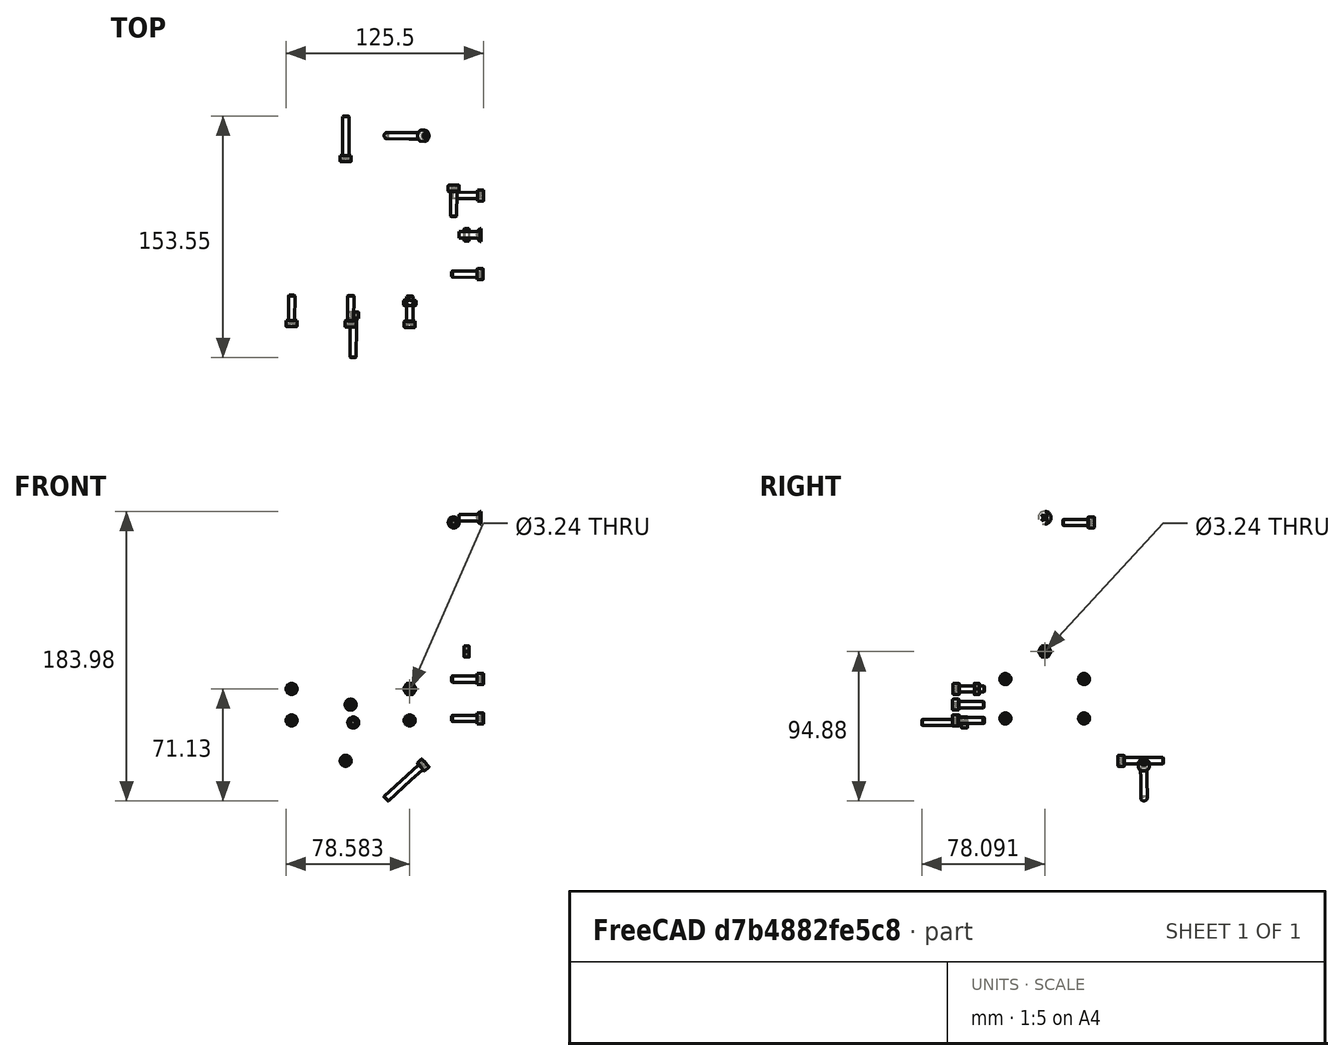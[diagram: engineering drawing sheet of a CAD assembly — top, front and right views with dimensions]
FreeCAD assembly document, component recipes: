
FREECAD ASSEMBLY — COMPONENT RECIPES ("RobotAssembly")

This assembly document has 52 components, labeled P0..P51 below (a component is one placed body or linked part). 4 of them carry a construction recipe — the FreeCAD feature program that regenerates the part from scratch, quoted from this document or its linked companion documents; the rest are supplied as boundary geometry only. No exploded tour is included for this assembly.
COMPONENT P0 — geometry summary ("Battery Mount"; no construction recipe available for this part):
  bounding box: 67.2 x 45.3 x 35.0 mm
  tessellated surface: 1,040 triangles
  volume: 39577 mm^3 (37% of its bounding box)
  symmetry: mirror-symmetric across its y mid-plane
COMPONENT P1 — geometry summary ("Bearing Wheel Mount"; no construction recipe available for this part):
  bounding box: 60.4 x 36.4 x 17.2 mm
  tessellated surface: 2,476 triangles
  volume: 15843 mm^3 (42% of its bounding box)
COMPONENT P2 — geometry summary ("Body"; no construction recipe available for this part):
  bounding box: 150.6 x 100.9 x 42.5 mm
  tessellated surface: 15,760 triangles
  volume: 188663 mm^3 (29% of its bounding box)
COMPONENT P3 — geometry summary ("Body Top"; no construction recipe available for this part):
  bounding box: 150.6 x 100.9 x 5.0 mm
  tessellated surface: 8,920 triangles
  volume: 66554 mm^3 (88% of its bounding box)
COMPONENT P4 — geometry summary ("Cat Toy Clamp"; no construction recipe available for this part):
  bounding box: 59.5 x 32.6 x 13.4 mm
  tessellated surface: 6,652 triangles
  volume: 22928 mm^3 (88% of its bounding box)
  symmetry: 2-fold rotationally symmetric about the x axis; mirror-symmetric across its z mid-plane
COMPONENT P5 — geometry summary ("Cat Toy Mount"; no construction recipe available for this part):
  bounding box: 100.1 x 95.0 x 49.3 mm
  tessellated surface: 9,540 triangles
  volume: 65342 mm^3 (14% of its bounding box)
  symmetry: mirror-symmetric across its y mid-plane
COMPONENT P6 — geometry summary ("Clamp"; no construction recipe available for this part):
  bounding box: 25.3 x 24.0 x 7.1 mm
  tessellated surface: 1,368 triangles
  volume: 1262 mm^3 (29% of its bounding box)
  symmetry: mirror-symmetric across its y mid-plane
COMPONENT P7 — geometry summary ("GUNCAIZHU_Ventilator_30x30x7,5_5V014"; no construction recipe available for this part):
  bounding box: 31.5 x 30.2 x 7.8 mm
  tessellated surface: 41,082 triangles
  volume: 3441 mm^3 (46% of its bounding box)
COMPONENT P8 — geometry summary ("am-3637 NeveRest Orbital 20 Gearmotor REV003"; no construction recipe available for this part):
  bounding box: 134.4 x 38.2 x 38.0 mm
  tessellated surface: 144,826 triangles
  volume: 110915 mm^3 (57% of its bounding box)
COMPONENT P9 — geometry summary ("M4x16-Screw026"; no construction recipe available for this part):
  bounding box: 20.0 x 7.0 x 7.0 mm
  tessellated surface: 5,082 triangles
  volume: 333 mm^3 (34% of its bounding box)
  symmetry: revolution-symmetric about the y axis through its bounding-box center; mirror-symmetric across its z mid-plane
COMPONENT P10 — geometry summary ("M4x14-Screw001"; no construction recipe available for this part):
  bounding box: 14.0 x 8.2 x 8.2 mm
  tessellated surface: 3,414 triangles
  volume: 224 mm^3 (24% of its bounding box)
  symmetry: mirror-symmetric across its y mid-plane, z mid-plane
COMPONENT P11 — geometry summary ("M4-Nut003"; no construction recipe available for this part):
  bounding box: 8.1 x 7.0 x 3.2 mm
  tessellated surface: 2,088 triangles
  volume: 107 mm^3 (58% of its bounding box)
COMPONENT P12 — geometry summary ("M4-Nut004"; no construction recipe available for this part):
  bounding box: 8.1 x 7.0 x 3.2 mm
  tessellated surface: 2,088 triangles
  volume: 107 mm^3 (58% of its bounding box)
  symmetry: 3-fold rotationally symmetric about the y axis
COMPONENT P13 — geometry summary ("M4-Nut006"; no construction recipe available for this part):
  bounding box: 8.1 x 7.0 x 3.2 mm
  tessellated surface: 2,088 triangles
  volume: 107 mm^3 (58% of its bounding box)
COMPONENT P14 — geometry summary ("M4-Nut007"; no construction recipe available for this part):
  bounding box: 8.1 x 7.0 x 3.2 mm
  tessellated surface: 2,088 triangles
  volume: 107 mm^3 (58% of its bounding box)
COMPONENT P15 — geometry summary ("M4-Nut008"; no construction recipe available for this part):
  bounding box: 8.1 x 7.0 x 3.2 mm
  tessellated surface: 2,088 triangles
  volume: 107 mm^3 (58% of its bounding box)
  symmetry: 3-fold rotationally symmetric about the y axis
COMPONENT P16 — geometry summary ("M4-Nut009"; no construction recipe available for this part):
  bounding box: 8.1 x 7.0 x 3.2 mm
  tessellated surface: 2,088 triangles
  volume: 107 mm^3 (58% of its bounding box)
COMPONENT P17 — geometry summary ("M4-Nut010"; no construction recipe available for this part):
  bounding box: 8.1 x 7.0 x 3.2 mm
  tessellated surface: 2,088 triangles
  volume: 107 mm^3 (58% of its bounding box)
COMPONENT P18 — geometry summary ("M4-Nut011"; no construction recipe available for this part):
  bounding box: 8.1 x 7.0 x 3.2 mm
  tessellated surface: 2,088 triangles
  volume: 107 mm^3 (58% of its bounding box)
  symmetry: 3-fold rotationally symmetric about the y axis
COMPONENT P19 — geometry summary ("M4-Nut012"; no construction recipe available for this part):
  bounding box: 8.1 x 7.0 x 3.2 mm
  tessellated surface: 2,088 triangles
  volume: 107 mm^3 (58% of its bounding box)
COMPONENT P20 — geometry summary ("M4x16-Screw034"; no construction recipe available for this part):
  bounding box: 20.0 x 7.0 x 7.0 mm
  tessellated surface: 5,082 triangles
  volume: 333 mm^3 (34% of its bounding box)
  symmetry: revolution-symmetric about the y axis through its bounding-box center; mirror-symmetric across its z mid-plane
COMPONENT P21 — geometry summary ("M4x16-Screw035"; no construction recipe available for this part):
  bounding box: 20.0 x 7.0 x 7.0 mm
  tessellated surface: 5,082 triangles
  volume: 333 mm^3 (34% of its bounding box)
  symmetry: revolution-symmetric about the y axis through its bounding-box center; mirror-symmetric across its z mid-plane
COMPONENT P22 — geometry summary ("M4x16-Screw036"; no construction recipe available for this part):
  bounding box: 20.0 x 7.0 x 7.0 mm
  tessellated surface: 5,082 triangles
  volume: 333 mm^3 (34% of its bounding box)
  symmetry: revolution-symmetric about the y axis through its bounding-box center; mirror-symmetric across its z mid-plane
COMPONENT P23 — geometry summary ("M4x16-Screw037"; no construction recipe available for this part):
  bounding box: 20.0 x 7.0 x 7.0 mm
  tessellated surface: 5,082 triangles
  volume: 333 mm^3 (34% of its bounding box)
  symmetry: revolution-symmetric about the y axis through its bounding-box center; mirror-symmetric across its z mid-plane
COMPONENT P24 — geometry summary ("M4x16-Screw038"; no construction recipe available for this part):
  bounding box: 20.0 x 7.0 x 7.0 mm
  tessellated surface: 5,082 triangles
  volume: 333 mm^3 (34% of its bounding box)
  symmetry: revolution-symmetric about the y axis through its bounding-box center; mirror-symmetric across its z mid-plane
COMPONENT P25 — geometry summary ("Motor Mount Right001"; no construction recipe available for this part):
  bounding box: 90.5 x 80.2 x 5.5 mm
  tessellated surface: 8,834 triangles
  volume: 22843 mm^3 (57% of its bounding box)
COMPONENT P26 — geometry summary ("Clamp001"; no construction recipe available for this part):
  bounding box: 28.4 x 10.2 x 7.1 mm
  tessellated surface: 1,368 triangles
  volume: 1262 mm^3 (61% of its bounding box)
  symmetry: mirror-symmetric across its y mid-plane
COMPONENT P27 — geometry summary ("Wheel001"; no construction recipe available for this part):
  bounding box: 55.0 x 55.0 x 21.6 mm
  tessellated surface: 19,376 triangles
  volume: 31320 mm^3 (48% of its bounding box)
COMPONENT P28 — geometry summary ("M4x30-Screw001"; no construction recipe available for this part):
  bounding box: 28.4 x 26.5 x 7.0 mm
  tessellated surface: 5,284 triangles
  volume: 509 mm^3 (10% of its bounding box)
COMPONENT P29 — geometry summary ("Bearing Wheel Mount001"; no construction recipe available for this part):
  bounding box: 60.4 x 36.4 x 17.2 mm
  tessellated surface: 2,476 triangles
  volume: 15843 mm^3 (42% of its bounding box)
COMPONENT P30 — geometry summary ("M4x16-Screw119"; no construction recipe available for this part):
  bounding box: 29.0 x 7.0 x 7.0 mm
  tessellated surface: 5,284 triangles
  volume: 446 mm^3 (31% of its bounding box)
  symmetry: revolution-symmetric about the y axis through its bounding-box center
COMPONENT P31 — geometry summary ("M4x16-Screw120"; no construction recipe available for this part):
  bounding box: 29.0 x 7.0 x 7.0 mm
  tessellated surface: 5,284 triangles
  volume: 446 mm^3 (31% of its bounding box)
  symmetry: revolution-symmetric about the y axis through its bounding-box center
COMPONENT P32 — geometry summary ("M4x16-Screw121"; no construction recipe available for this part):
  bounding box: 29.0 x 7.0 x 7.0 mm
  tessellated surface: 5,284 triangles
  volume: 446 mm^3 (31% of its bounding box)
  symmetry: revolution-symmetric about the y axis through its bounding-box center
COMPONENT P33 — geometry summary ("M4x16-Screw123"; no construction recipe available for this part):
  bounding box: 29.0 x 7.0 x 7.0 mm
  tessellated surface: 5,284 triangles
  volume: 446 mm^3 (31% of its bounding box)
COMPONENT P34 — geometry summary ("1609-0613-0008"; no construction recipe available for this part):
  bounding box: 13.0 x 13.0 x 6.1 mm
  tessellated surface: 16,484 triangles
  volume: 513 mm^3 (50% of its bounding box)
  symmetry: 2-fold rotationally symmetric about the x axis; revolution-symmetric about the y axis through its bounding-box center; 2-fold rotationally symmetric about the z axis; mirror-symmetric across its x mid-plane, y mid-plane, z mid-plane
COMPONENT P35 — geometry summary ("StringGuard001"; no construction recipe available for this part):
  bounding box: 15.0 x 12.5 x 8.1 mm
  tessellated surface: 2,628 triangles
  volume: 615 mm^3 (40% of its bounding box)
  symmetry: 2-fold rotationally symmetric about the z axis; mirror-symmetric across its x mid-plane, y mid-plane
COMPONENT P36 — geometry summary ("am-3637 NeveRest Orbital 20 Gearmotor REV004"; no construction recipe available for this part):
  bounding box: 134.4 x 38.2 x 38.0 mm
  tessellated surface: 144,826 triangles
  volume: 110915 mm^3 (57% of its bounding box)
COMPONENT P37 — geometry summary ("Motor Mount Right"; no construction recipe available for this part):
  bounding box: 90.5 x 80.2 x 5.5 mm
  tessellated surface: 8,834 triangles
  volume: 22843 mm^3 (57% of its bounding box)
COMPONENT P38 — geometry summary ("Passive Claw Left"; no construction recipe available for this part):
  bounding box: 57.6 x 35.3 x 21.5 mm
  tessellated surface: 2,676 triangles
  volume: 8897 mm^3 (20% of its bounding box)
COMPONENT P39 — geometry summary ("Passive Claw Right"; no construction recipe available for this part):
  bounding box: 57.6 x 35.3 x 21.5 mm
  tessellated surface: 2,676 triangles
  volume: 8897 mm^3 (20% of its bounding box)
COMPONENT P40 — geometry summary ("Ras Pi 3B+179"; no construction recipe available for this part):
  bounding box: 89.4 x 58.8 x 19.1 mm
  tessellated surface: 24,256 triangles
  volume: 25288 mm^3 (25% of its bounding box)
COMPONENT P41 — recipe-attached ("SAR2-20_b", a linked part whose construction recipe lives in a companion FreeCAD document of the same project; that document's serialized recipe follows).
Construction recipe (the companion document, serialized — sketch geometry with constraints, then the solid features built on it; lengths are millimeters unless a unit is written):

FCSTD DOCUMENT  (FreeCAD 1.1R42987 (Git))
Label: MISUMI-Sar220
License: All rights reserved
LicenseURL: https://en.wikipedia.org/wiki/All_rights_reserved
objects: Part::Feature×2, Part::DatumPoint×2
note: 2 computed .brp shape members not serialized (recipe doc carries the construction recipe); baked Part::Feature solids carry a one-line shape summary decoded from their .brp

FEATURE [Part::Feature] Part__Feature  label="SAR2-20_r"
  Placement = pos=(1.89152,0.668144,-0.306396) rot=(0,0,1;0rad)
  shape: bbox 5.8 x 12.1 x 200 mm, 38 faces (baked)
FEATURE [Part::Feature] Part__Feature001  label="SAR2-20_b"
  Placement = pos=(7.09149,-3.28186,-0.306396) rot=(0,0,1;0rad)
  shape: bbox 7.4 x 20 x 200 mm, 93 faces (baked)
FEATURE [Part::DatumPoint] DatumPoint
  AttacherType = Attacher::AttachEnginePoint
  AttachmentSupport = -> [Part__Feature001]
  MapMode = 37
  Placement = pos=(2.19373,6.71814,199.694) rot=(0,0,1;0rad)
FEATURE [Part::DatumPoint] DatumPoint001
  AttacherType = Attacher::AttachEnginePoint
  AttachmentSupport = -> [Part__Feature]
  MapMode = 37
  Placement = pos=(5.18893,6.71814,199.694) rot=(0,0,1;0rad)
COMPONENT P42 — same part as P41; its construction recipe is shown at P41.
COMPONENT P43 — geometry summary ("Slides Motor Mount"; no construction recipe available for this part):
  bounding box: 57.1 x 55.0 x 36.3 mm
  tessellated surface: 7,668 triangles
  volume: 23194 mm^3 (20% of its bounding box)
  symmetry: mirror-symmetric across its x mid-plane
COMPONENT P44 — geometry summary ("Slides Mount"; no construction recipe available for this part):
  bounding box: 139.5 x 60.0 x 25.1 mm
  tessellated surface: 4,146 triangles
  volume: 36849 mm^3 (18% of its bounding box)
COMPONENT P45 — geometry summary ("Slides Plate"; no construction recipe available for this part):
  bounding box: 189.0 x 78.0 x 5.5 mm
  tessellated surface: 4,636 triangles
  volume: 36980 mm^3 (46% of its bounding box)
  symmetry: mirror-symmetric across its x mid-plane
COMPONENT P46 — geometry summary ("Spool"; no construction recipe available for this part):
  bounding box: 35.2 x 35.2 x 35.0 mm
  tessellated surface: 8,372 triangles
  volume: 14357 mm^3 (33% of its bounding box)
COMPONENT P47 — recipe-attached ("Spool CHub", a linked part whose construction recipe lives in a companion FreeCAD document of the same project; that document's serialized recipe follows).
Construction recipe (the companion document, serialized — sketch geometry with constraints, then the solid features built on it; lengths are millimeters unless a unit is written):

FCSTD DOCUMENT  (FreeCAD 1.1R42863 (Git))
Label: Spool
License: All rights reserved
LicenseURL: https://en.wikipedia.org/wiki/All_rights_reserved
objects: Sketcher::SketchObject×7, PartDesign::Pad×5, App::Point×2, PartDesign::Pocket×2, PartDesign::Chamfer×2, PartDesign::Body×2, Part::DatumPlane×1, PartDesign::PolarPattern×1, PartDesign::SubShapeBinder×1, PartDesign::Fillet×1
note: 49 computed .brp shape members not serialized (recipe doc carries the construction recipe); baked Part::Feature solids carry a one-line shape summary decoded from their .brp
EXTERNAL_REF file=../Variables.FCStd obj=Spreadsheet

FEATURE [App::Point] Origin001
  Role = Origin
FEATURE [Sketcher::SketchObject] Sketch
  ArcFitTolerance = 1e-06
  AttachmentSupport = -> [XY_Plane]
  ExternalTypes = [0]
  FullyConstrained = true
  MakeInternals = false
  MapMode = 5
  expr: Constraints[13] = Variables#Spreadsheet.SpoolInnerDiam
  expr: Constraints[7] = Variables#Spreadsheet.M4TapDiam
  sketch-geometry (7):
    g0: Circle CenterX=-2.798e-13 CenterY=0 CenterZ=0 NormalX=0 NormalY=0 NormalZ=1 AngleXU=0 Radius=17.5
    g1: LineSegment [constr] StartX=9 StartY=5 StartZ=0 EndX=9 EndY=-5 EndZ=0
    g2: GeomPoint [constr] X=9 Y=0 Z=0
    g3: Circle CenterX=9 CenterY=5 CenterZ=0 NormalX=0 NormalY=0 NormalZ=1 AngleXU=0 Radius=1.8
    g4: Circle CenterX=9 CenterY=-5 CenterZ=0 NormalX=0 NormalY=0 NormalZ=1 AngleXU=0 Radius=1.8
    g5: Circle CenterX=-2.798e-13 CenterY=0 CenterZ=0 NormalX=0 NormalY=0 NormalZ=1 AngleXU=0 Radius=3.125
    g6: Circle [constr] CenterX=-2.798e-13 CenterY=0 CenterZ=0 NormalX=0 NormalY=0 NormalZ=1 AngleXU=0 Radius=7.5
  constraints (15):
    c: Diameter(g0) = 35
    c: Coincident(g0,g-1)
    c: Distance(g1) = 10
    c: Vertical(g1)
    c: Symmetric(g1,g1,g2)
    c: PointOnObject(g2,g-1)
    c: Coincident(g3,g1)
    c: Diameter(g3) = 3.6
    c: Coincident(g4,g1)
    c: Equal(g4,g3)
    c: Diameter(g5) = 6.25
    c: Coincident(g5,g0)
    c: Coincident(g6,g0)
    c: Diameter(g6) = 15
    c: Distance(g2,g6) = 1.5
FEATURE [PartDesign::Pad] Pad
  Direction = (0,0,1)
  Length = 5
  Length2 = 10
  Profile = -> Sketch
  ReferenceAxis = -> Sketch [N_Axis]
  Refine = true
  Suppressed = false
  Type = 0
  expr: Length = Variables#Spreadsheet.SpoolWallThickness
FEATURE [Sketcher::SketchObject] Sketch001
  ArcFitTolerance = 1e-06
  AttachmentSupport = -> [Pad]
  ExternalGeometry = -> [Pad]
  ExternalTypes = [0]
  FullyConstrained = true
  MakeInternals = false
  MapMode = 5
  Placement = pos=(0,0,0) rot=(1,0,0;3.14159rad)
  expr: Constraints[0] = Variables#Spreadsheet.SpoolInnerDiam
  sketch-geometry (1):
    g0: Circle CenterX=0 CenterY=0 CenterZ=0 NormalX=0 NormalY=0 NormalZ=1 AngleXU=0 Radius=7.5
  constraints (2):
    c: Diameter(g0) = 15
    c: Coincident(g0,g-1)
FEATURE [PartDesign::Pad] Pad001
  BaseFeature = -> Pad
  Direction = (0,0,-1)
  Length = 35
  Length2 = 10
  Profile = -> Sketch001
  ReferenceAxis = -> Sketch001 [N_Axis]
  Refine = true
  Reversed = true
  Suppressed = false
  Type = 0
  expr: Length = Variables#Spreadsheet.SpoolThickness
FEATURE [Sketcher::SketchObject] Sketch002
  ArcFitTolerance = 1e-06
  AttachmentSupport = -> [Pad001]
  ExternalGeometry = -> [Pad001]
  ExternalTypes = [0,0]
  FullyConstrained = true
  MakeInternals = false
  MapMode = 5
  Placement = pos=(0,0,35) rot=(0,0,1;0rad)
FEATURE [PartDesign::Pad] Pad002
  BaseFeature = -> Pad001
  Direction = (0,0,1)
  Length = 5
  Length2 = 10
  Profile = -> Sketch002
  ReferenceAxis = -> Sketch002 [N_Axis]
  Refine = true
  Reversed = true
  Suppressed = false
  Type = 0
  expr: Length = Variables#Spreadsheet.SpoolWallThickness
FEATURE [Part::DatumPlane] DatumPlane
  AttachmentSupport = -> [Pad002]
  MapMode = 45
  Placement = pos=(-9e-16,0,17.5) rot=(0,0,1;0rad)
FEATURE [Sketcher::SketchObject] Sketch003
  ArcFitTolerance = 1e-06
  AttachmentSupport = -> [DatumPlane]
  ExternalGeometry = -> [Pad002]
  ExternalTypes = [0,0]
  FullyConstrained = true
  MakeInternals = false
  MapMode = 5
  Placement = pos=(-9e-16,0,17.5) rot=(0,0,1;0rad)
FEATURE [PartDesign::Pad] Pad003
  BaseFeature = -> Pad002
  Direction = (0,0,1)
  Length = 5
  Length2 = 10
  Midplane = true
  Profile = -> Sketch003
  ReferenceAxis = -> Sketch003 [N_Axis]
  Refine = true
  Suppressed = false
  Type = 0
  expr: Length = Variables#Spreadsheet.SpoolWallThickness
FEATURE [Sketcher::SketchObject] Sketch004
  ArcFitTolerance = 1e-06
  AttachmentSupport = -> [Pad003]
  ExternalGeometry = -> [Pad003]
  ExternalTypes = [0,0]
  FullyConstrained = true
  MakeInternals = false
  MapMode = 5
  Placement = pos=(0,0,20) rot=(0,0,1;0rad)
  sketch-geometry (5):
    g0: LineSegment [constr] StartX=9.5 StartY=-3 StartZ=0 EndX=9.5 EndY=3 EndZ=0
    g1: Circle CenterX=9.5 CenterY=-3 CenterZ=0 NormalX=0 NormalY=0 NormalZ=1 AngleXU=0 Radius=1.75
    g2: Circle CenterX=9.5 CenterY=3 CenterZ=0 NormalX=0 NormalY=0 NormalZ=1 AngleXU=0 Radius=1.75
    g3: GeomPoint [constr] X=7.5 Y=0 Z=0
    g4: GeomPoint [constr] X=9.5 Y=0 Z=0
  constraints (11):
    c: Vertical(g0)
    c: DistanceY(g0,g0) = 6
    c: Diameter(g1) = 3.5
    c: Coincident(g1,g0)
    c: Coincident(g2,g0)
    c: Equal(g1,g2)
    c: PointOnObject(g3,g-3)
    c: Symmetric(g0,g0,g4)
    c: PointOnObject(g3,g-1)
    c: PointOnObject(g4,g-1)
    c: DistanceX(g3,g4) = 2
FEATURE [PartDesign::Pocket] Pocket
  BaseFeature = -> Pad003
  Direction = (0,0,-1)
  Length = 0
  Length2 = 5
  Profile = -> Sketch004
  ReferenceAxis = -> Sketch004 [N_Axis]
  Refine = true
  Suppressed = false
  Type = 3
  UpToFace = -> Pad003 [Face10]
FEATURE [PartDesign::PolarPattern] PolarPattern
  Angle = 360
  Axis = -> Sketch004 [N_Axis]
  BaseFeature = -> Pocket
  Mode = 0
  Occurrences = 4
  Offset = 120
  Originals = -> [Pocket]
  Refine = true
  Suppressed = false
  TransformMode = 0
FEATURE [PartDesign::Chamfer] Chamfer
  Angle = 45
  Base = -> PolarPattern [Edge19,Edge30]
  BaseFeature = -> PolarPattern
  ChamferType = 0
  FlipDirection = false
  Refine = true
  Size = 2
  Size2 = 1
  SupportTransform = false
  Suppressed = false
  UseAllEdges = false
  expr: Size = Variables#Spreadsheet.SpoolWallThickness / 2 - 0.5
FEATURE [PartDesign::Chamfer] Chamfer001
  Angle = 45
  Base = -> Chamfer [Edge35,Edge41]
  BaseFeature = -> Chamfer
  ChamferType = 0
  FlipDirection = false
  Refine = true
  Size = 4
  Size2 = 1
  SupportTransform = false
  Suppressed = false
  UseAllEdges = false
  expr: Size = Variables#Spreadsheet.SpoolWallThickness - 1
FEATURE [PartDesign::Body] Body  label="Spool"
  AllowCompound = true
  Group = -> [Sketch,Pad,Sketch001,Pad001,Sketch002,Pad002,DatumPlane,Sketch003,Pad003,Sketch004,Pocket,PolarPattern,Chamfer,Chamfer001]
  Origin = -> Origin
  Tip = -> Chamfer001
FEATURE [App::Point] Origin003
  Role = Origin
FEATURE [PartDesign::SubShapeBinder] Binder
  BindCopyOnChange = 0
  BindMode = 0
  ClaimChildren = false
  Context = -> Body001 [Binder.]
  Fuse = false
  MakeFace = true
  OffsetFill = false
  OffsetIntersection = false
  OffsetJoinType = 0
  OffsetOpenResult = false
  PartialLoad = false
  Refine = true
  Relative = true
  Support = -> [Body]
  _Version = 2
FEATURE [Sketcher::SketchObject] Sketch005
  ArcFitTolerance = 1e-06
  AttachmentSupport = -> [Binder]
  ExternalGeometry = -> [Binder]
  ExternalTypes = [0,0,0]
  FullyConstrained = false
  MakeInternals = false
  MapMode = 5
  Placement = pos=(0,0,0) rot=(1,0,0;3.14159rad)
  expr: Constraints[34] = Variables#Spreadsheet.M4ThroughBoreDiam
  sketch-geometry (16):
    g0: ArcOfCircle CenterX=9 CenterY=5 CenterZ=0 NormalX=0 NormalY=0 NormalZ=1 AngleXU=0 Radius=4 StartAngle=-9e-16 EndAngle=1.90109
    g1: ArcOfCircle CenterX=9 CenterY=-5 CenterZ=0 NormalX=0 NormalY=0 NormalZ=1 AngleXU=0 Radius=4 StartAngle=4.38209 EndAngle=6.28319
    g2: LineSegment StartX=13 StartY=-5 StartZ=0 EndX=13 EndY=5 EndZ=0
    g3: LineSegment StartX=-11.5 StartY=7 StartZ=0 EndX=2.5 EndY=7 EndZ=0
    g4: LineSegment StartX=2.5 StartY=7 StartZ=0 EndX=7.7027 EndY=8.78378 EndZ=0
    g5: LineSegment StartX=-11.5 StartY=-7 StartZ=0 EndX=2.5 EndY=-7 EndZ=0
    g6: LineSegment StartX=2.5 StartY=-7 StartZ=0 EndX=7.7027 EndY=-8.78378 EndZ=0
    g7: GeomPoint X=0.731343 Y=-5.50967 Z=0
    g8: LineSegment StartX=-11.5 StartY=-7 StartZ=0 EndX=-11.5 EndY=-1.5 EndZ=0
    g9: ArcOfCircle CenterX=0 CenterY=0 CenterZ=0 NormalX=0 NormalY=0 NormalZ=1 AngleXU=0 Radius=3.075 StartAngle=3.65117 EndAngle=8.9152
    g10: LineSegment StartX=-11.5 StartY=7 StartZ=0 EndX=-11.5 EndY=1.5 EndZ=0
    g11: LineSegment StartX=-11.5 StartY=1.5 StartZ=0 EndX=-2.68433 EndY=1.5 EndZ=0
    g12: LineSegment StartX=-11.5 StartY=-1.5 StartZ=0 EndX=-2.68433 EndY=-1.5 EndZ=0
    g13: GeomPoint X=-11.5 Y=0 Z=0
    g14: Circle CenterX=9 CenterY=5 CenterZ=0 NormalX=0 NormalY=0 NormalZ=1 AngleXU=0 Radius=2.175
    g15: Circle CenterX=9 CenterY=-5 CenterZ=0 NormalX=0 NormalY=0 NormalZ=1 AngleXU=0 Radius=2.175
  constraints (37):
    c: Coincident(g0,g-3)
    c: Coincident(g1,g-4)
    c: Tangent(g2,g1) = -1.5708
    c: Tangent(g2,g0) = -1.5708
    c: Vertical(g2)
    c: Horizontal(g3)
    c: Coincident(g4,g3)
    c: Horizontal(g5)
    c: Coincident(g6,g5)
    c: Tangent(g6,g1) = -1.5708
    c: Tangent(g4,g0) = 1.5708
    c: Vertical(g3,g5)
    c: Vertical(g5,g3)
    c: Equal(g4,g6)
    c: DistanceX(g5,g5) = 14
    c: Distance(g5,g-2) = 2.5
    c: Coincident(g8,g5)
    c: Vertical(g8)
    c: Coincident(g9,g-1)
    c: Horizontal(g9,g8)
    c: Coincident(g10,g3)
    c: Vertical(g10)
    c: Coincident(g11,g10)
    c: Horizontal(g11)
    c: Coincident(g12,g8)
    c: Coincident(g12,g9)
    c: PointOnObject(g13,g-1)
    c: Symmetric(g10,g8,g13)
    c: Distance(g11,g12) = 3
    c: Distance(g3,g5) = 14
    c: Radius(g0) = 4
    c: Coincident(g9,g11)
    c: Radius(g9) = 3.075
    c: Coincident(g14,g0)
    c: Diameter(g14) = 4.35
    c: Coincident(g15,g1)
    c: Equal(g14,g15)
FEATURE [PartDesign::Pad] Pad004
  Direction = (0,0,-1)
  Length = 9
  Length2 = 10
  Profile = -> Sketch005
  ReferenceAxis = -> Sketch005 [N_Axis]
  Refine = true
  Suppressed = false
  Type = 0
FEATURE [Sketcher::SketchObject] Sketch006
  ArcFitTolerance = 1e-06
  AttachmentSupport = -> [Pad004]
  ExternalGeometry = -> [Pad004]
  ExternalTypes = [0]
  FullyConstrained = true
  MakeInternals = false
  MapMode = 5
  Placement = pos=(0,7,0) rot=(0,0.707107,0.707107;3.14159rad)
  expr: Constraints[1] = Variables#Spreadsheet.M4ThroughBoreDiam
  sketch-geometry (2):
    g0: GeomPoint [constr] X=11.5 Y=-4.5 Z=0
    g1: Circle CenterX=7.5 CenterY=-4.5 CenterZ=0 NormalX=0 NormalY=0 NormalZ=1 AngleXU=0 Radius=2.175
  constraints (4):
    c: Symmetric(g-3,g-3,g0)
    c: Diameter(g1) = 4.35
    c: Horizontal(g1,g0)
    c: DistanceX(g1,g0) = 4
FEATURE [PartDesign::Pocket] Pocket001
  BaseFeature = -> Pad004
  Direction = (0,-1,2e-16)
  Length = 0
  Length2 = 5
  Profile = -> Sketch006
  ReferenceAxis = -> Sketch006 [N_Axis]
  Refine = true
  Suppressed = false
  Type = 3
  UpToFace = -> Pad004 [Face7]
FEATURE [PartDesign::Fillet] Fillet
  Base = -> Pocket001 [Edge41,Edge43,Edge6,Edge1]
  BaseFeature = -> Pocket001
  Radius = 0.75
  Refine = true
  SupportTransform = false
  Suppressed = false
  UseAllEdges = false
FEATURE [PartDesign::Body] Body001  label="Spool CHub"
  AllowCompound = true
  Group = -> [Binder,Sketch005,Pad004,Sketch006,Pocket001,Fillet]
  Origin = -> Origin002
  Tip = -> Fillet
COMPONENT P48 — geometry summary ("StringGuard"; no construction recipe available for this part):
  bounding box: 15.0 x 12.5 x 8.1 mm
  tessellated surface: 2,628 triangles
  volume: 615 mm^3 (40% of its bounding box)
  symmetry: 2-fold rotationally symmetric about the z axis; mirror-symmetric across its y mid-plane
COMPONENT P49 — geometry summary ("Wheel"; no construction recipe available for this part):
  bounding box: 55.0 x 55.0 x 21.8 mm
  tessellated surface: 19,376 triangles
  volume: 31320 mm^3 (48% of its bounding box)
COMPONENT P50 — recipe-attached ("1609-0613-0007", a linked part whose construction recipe lives in a companion FreeCAD document of the same project; that document's serialized recipe follows).
Construction recipe (the companion document, serialized — sketch geometry with constraints, then the solid features built on it; lengths are millimeters unless a unit is written):

FCSTD DOCUMENT  (FreeCAD 1.1R42987 (Git))
Label: V-Groove
License: All rights reserved
LicenseURL: https://en.wikipedia.org/wiki/All_rights_reserved
objects: Sketcher::SketchObject×5, PartDesign::Pad×4, Part::Feature×3, App::Point×2, App::Part×1, PartDesign::SubShapeBinder×1, Part::DatumPlane×1, PartDesign::Pocket×1, PartDesign::Mirrored×1, PartDesign::Body×1
note: 32 computed .brp shape members not serialized (recipe doc carries the construction recipe); baked Part::Feature solids carry a one-line shape summary decoded from their .brp
EXTERNAL_REF file=../Variables.FCStd obj=Spreadsheet

FEATURE [Part::Feature] Part__Feature  label="1609-0613-0004"
  shape: bbox 9.277 x 0.3004 x 9.277 mm, 8 faces (baked)
FEATURE [Part::Feature] Part__Feature001  label="1609-0613-0005"
  shape: bbox 9.277 x 0.3004 x 9.277 mm, 8 faces (baked)
FEATURE [Part::Feature] Part__Feature002  label="1609-0613-0006"
  shape: bbox 13 x 6 x 13 mm, 66 faces (baked)
FEATURE [App::Part] _609_0613_0004  label="1609-0613-0007"
  Group = -> [Part__Feature,Part__Feature001,Part__Feature002]
  Origin = -> Origin
FEATURE [App::Point] Origin001
  Role = Origin
FEATURE [App::Point] Origin003
  Role = Origin
FEATURE [PartDesign::SubShapeBinder] Binder
  BindCopyOnChange = 0
  BindMode = 0
  ClaimChildren = false
  Context = -> Body [Binder.]
  Fuse = false
  MakeFace = true
  OffsetFill = false
  OffsetIntersection = false
  OffsetJoinType = 0
  OffsetOpenResult = false
  PartialLoad = false
  Refine = true
  Relative = true
  Support = -> [_609_0613_0004]
  _Version = 2
FEATURE [Sketcher::SketchObject] Sketch
  ArcFitTolerance = 1e-06
  AttachmentOffset = pos=(0,0,0.25) rot=(0,0,1;0rad)
  AttachmentSupport = -> [Binder]
  ExternalTypes = [0]
  FullyConstrained = true
  MakeInternals = false
  MapMode = 5
  Placement = pos=(0,-0.25,1e-16) rot=(1,0,0;1.5708rad)
  expr: Constraints[1] = Variables#Spreadsheet.M4ThroughBoreDiam
  sketch-geometry (2):
    g0: Circle CenterX=0 CenterY=0 CenterZ=0 NormalX=0 NormalY=0 NormalZ=1 AngleXU=0 Radius=2.175
    g1: Circle CenterX=0 CenterY=0 CenterZ=0 NormalX=0 NormalY=0 NormalZ=1 AngleXU=0 Radius=2.75
  constraints (4):
    c: Coincident(g0,g-1)
    c: Diameter(g0) = 4.35
    c: Coincident(g1,g0)
    c: Diameter(g1) = 5.5
FEATURE [PartDesign::Pad] Pad
  Direction = (0,-1,2e-16)
  Length = 1
  Length2 = 10
  Profile = -> Sketch
  ReferenceAxis = -> Sketch [N_Axis]
  Refine = true
  Suppressed = false
  Type = 0
FEATURE [Sketcher::SketchObject] Sketch001
  ArcFitTolerance = 1e-06
  AttachmentSupport = -> [Pad]
  ExternalGeometry = -> [Pad]
  ExternalTypes = [0]
  FullyConstrained = true
  MakeInternals = false
  MapMode = 5
  Placement = pos=(0,-1.25,3e-16) rot=(1,0,0;1.5708rad)
  sketch-geometry (4):
    g0: ArcOfCircle CenterX=0 CenterY=-4.3033e-12 CenterZ=0 NormalX=0 NormalY=0 NormalZ=1 AngleXU=0 Radius=4 StartAngle=3.14159 EndAngle=6.28319
    g1: LineSegment StartX=4 StartY=-6.67326e-11 StartZ=0 EndX=4 EndY=8 EndZ=0
    g2: LineSegment StartX=4 StartY=8 StartZ=0 EndX=-4 EndY=8 EndZ=0
    g3: LineSegment StartX=-4 StartY=8 StartZ=0 EndX=-4 EndY=-7.6463e-12 EndZ=0
  constraints (10):
    c: Coincident(g0,g-1)
    c: Vertical(g1)
    c: Coincident(g2,g1)
    c: Horizontal(g2)
    c: Coincident(g3,g2)
    c: Vertical(g3)
    c: DistanceY(g1,g1) = 8
    c: Diameter(g0) = 8
    c: Tangent(g1,g0) = -1.5708
    c: Tangent(g3,g0) = -1.5708
FEATURE [PartDesign::Pad] Pad001
  BaseFeature = -> Pad
  Direction = (0,-1,2e-16)
  Length = 2
  Length2 = 10
  Profile = -> Sketch001
  ReferenceAxis = -> Sketch001 [N_Axis]
  Refine = true
  Suppressed = false
  Type = 0
FEATURE [Sketcher::SketchObject] Sketch002
  ArcFitTolerance = 1e-06
  AttachmentSupport = -> [Pad001]
  ExternalGeometry = -> [Pad001]
  ExternalTypes = [0]
  FullyConstrained = true
  MakeInternals = false
  MapMode = 5
  Placement = pos=(0,-3.25,0) rot=(1,0,0;1.5708rad)
  sketch-geometry (3):
    g0: LineSegment StartX=-4 StartY=8 StartZ=0 EndX=-4 EndY=11 EndZ=0
    g1: LineSegment StartX=-4 StartY=11 StartZ=0 EndX=4 EndY=11 EndZ=0
    g2: LineSegment StartX=4 StartY=11 StartZ=0 EndX=4 EndY=8 EndZ=0
  constraints (8):
    c: Coincident(g-3,g0)
    c: Vertical(g0)
    c: Coincident(g0,g1)
    c: Horizontal(g1)
    c: Coincident(g1,g2)
    c: Coincident(g2,g-3)
    c: Vertical(g2)
    c: DistanceY(g2,g2) = 3
FEATURE [Part::DatumPlane] Plane
  AttachmentSupport = -> [Binder]
  MapMode = 11
  Placement = pos=(0,3,0) rot=(0,0.707107,0.707107;3.14159rad)
FEATURE [PartDesign::Pad] Pad002
  BaseFeature = -> Pad001
  Direction = (0,-1,2e-16)
  Length = 10
  Length2 = 10
  Profile = -> Sketch002
  ReferenceAxis = -> Sketch002 [N_Axis]
  Refine = true
  Suppressed = false
  Type = 3
  UpToFace = -> Plane
FEATURE [Sketcher::SketchObject] Sketch003
  ArcFitTolerance = 1e-06
  AttachmentSupport = -> [Pad002]
  ExternalGeometry = -> [Pad002]
  ExternalTypes = [0,0]
  FullyConstrained = true
  MakeInternals = false
  MapMode = 5
  Placement = pos=(-4,0,0) rot=(0.57735,-0.57735,-0.57735;2.0944rad)
  sketch-geometry (3):
    g0: LineSegment StartX=0.25 StartY=8 StartZ=0 EndX=1.25 EndY=8 EndZ=0
    g1: LineSegment StartX=1.25 StartY=8 StartZ=0 EndX=1.25 EndY=7 EndZ=0
    g2: ArcOfCircle CenterX=0.25 CenterY=7 CenterZ=0 NormalX=0 NormalY=0 NormalZ=1 AngleXU=0 Radius=1 StartAngle=-4.805e-13 EndAngle=1.5708
  constraints (7):
    c: PointOnObject(g0,g-3)
    c: Coincident(g0,g-4)
    c: Coincident(g0,g1)
    c: PointOnObject(g1,g-4)
    c: Tangent(g2,g0) = 1.5708
    c: Tangent(g2,g1) = 1.5708
    c: Radius(g2) = 1
FEATURE [PartDesign::Pad] Pad003
  BaseFeature = -> Pad002
  Direction = (-1,0,0)
  Length = 10
  Length2 = 10
  Profile = -> Sketch003
  ReferenceAxis = -> Sketch003 [N_Axis]
  Refine = true
  Suppressed = false
  Type = 3
  UpToFace = -> Pad002 [Face10]
FEATURE [Sketcher::SketchObject] Sketch004
  ArcFitTolerance = 1e-06
  AttachmentSupport = -> [Pad003]
  ExternalGeometry = -> [Pad003]
  ExternalTypes = [0,0,0]
  FullyConstrained = true
  MakeInternals = false
  MapMode = 5
  Placement = pos=(-4,0,0) rot=(0.57735,-0.57735,-0.57735;2.0944rad)
  sketch-geometry (3):
    g0: LineSegment StartX=2.25 StartY=11 StartZ=0 EndX=3.25 EndY=11 EndZ=0
    g1: LineSegment StartX=3.25 StartY=11 StartZ=0 EndX=3.25 EndY=10 EndZ=0
    g2: ArcOfCircle CenterX=2.25 CenterY=10 CenterZ=0 NormalX=0 NormalY=0 NormalZ=1 AngleXU=0 Radius=1 StartAngle=-3.624e-13 EndAngle=1.5708
  constraints (7):
    c: PointOnObject(g0,g-3)
    c: Coincident(g0,g-4)
    c: Coincident(g0,g1)
    c: PointOnObject(g1,g-4)
    c: Tangent(g2,g0) = 1.5708
    c: Tangent(g2,g1) = 1.5708
    c: Equal(g-5,g2)
FEATURE [PartDesign::Pocket] Pocket
  BaseFeature = -> Pad003
  Direction = (1,0,0)
  Length = 0
  Length2 = 5
  Profile = -> Sketch004
  ReferenceAxis = -> Sketch004 [N_Axis]
  Refine = true
  Suppressed = false
  Type = 3
  UpToFace = -> Pad003 [Face11]
FEATURE [PartDesign::Mirrored] Mirrored
  BaseFeature = -> Pocket
  MirrorPlane = -> Pad002 [Face7]
  Refine = true
  Suppressed = false
  TransformMode = 1
FEATURE [PartDesign::Body] Body  label="StringGuard"
  AllowCompound = true
  Group = -> [Binder,Sketch,Pad,Sketch001,Pad001,Sketch002,Plane,Pad002,Sketch003,Pad003,Sketch004,Pocket,Mirrored]
  Origin = -> Origin002
  Tip = -> Mirrored
COMPONENT P51 — geometry summary ("am-3637 NeveRest Orbital 20 Gearmotor REV2"; no construction recipe available for this part):
  bounding box: 134.4 x 38.2 x 38.0 mm
  tessellated surface: 144,826 triangles
  volume: 110915 mm^3 (57% of its bounding box)
PROVENANCE & LICENSES
A FreeCAD (.FCStd) document from a public repository crawl; recipes are the document's own serialized feature recipes (and, for linked parts, companion documents' recipes).
License: as declared in the source repository (recorded in the dataset sidecar).
